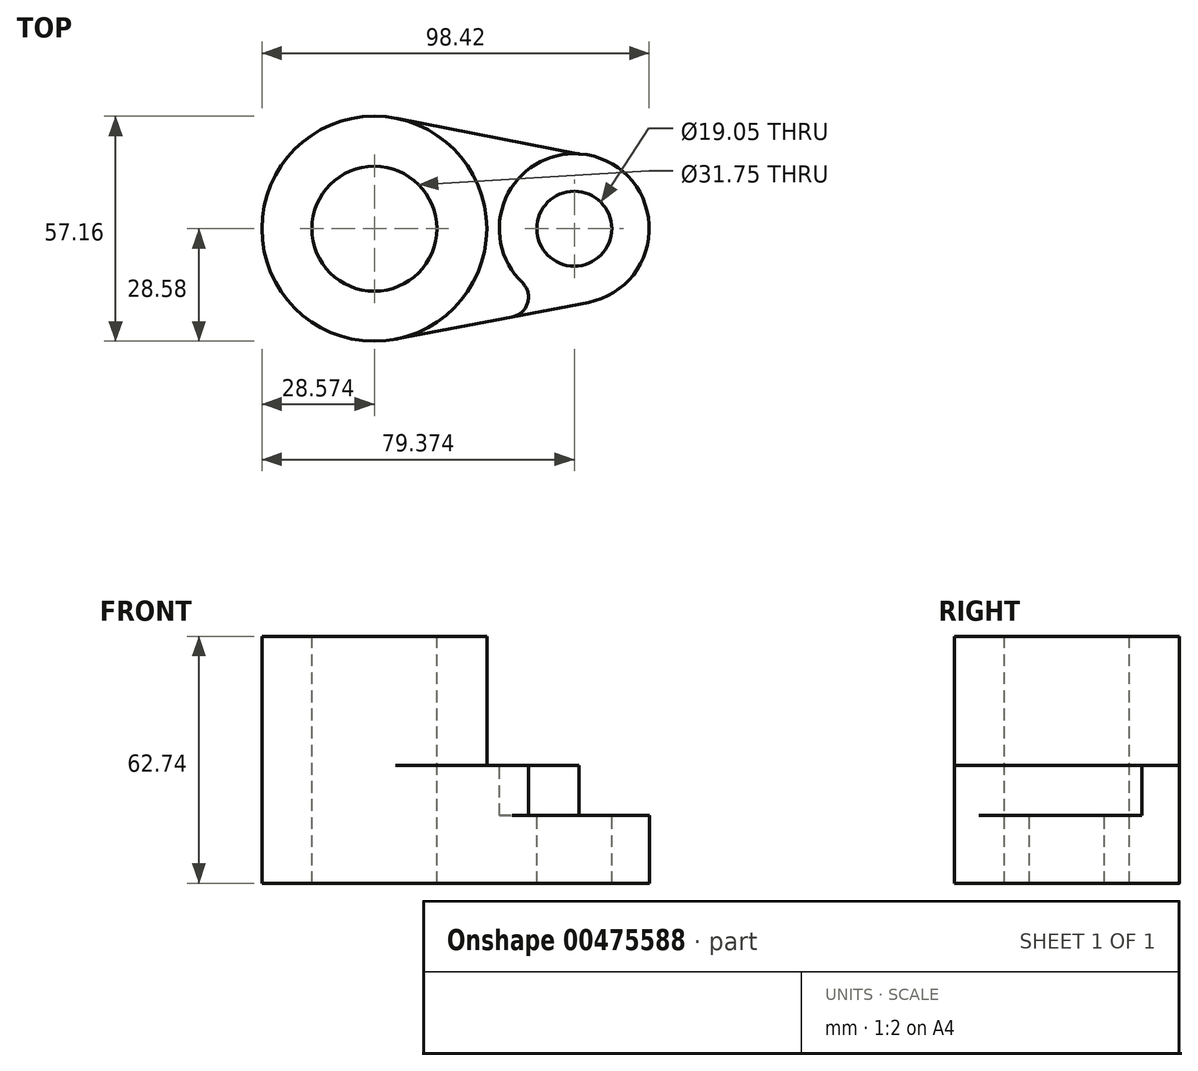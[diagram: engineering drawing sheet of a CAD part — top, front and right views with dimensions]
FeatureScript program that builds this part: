
annotation { "Feature Type Name" : "Feature", "Feature Type Description" : "" }
export const myFeature = defineFeature(function(context is Context, id is Id, definition is map)
    precondition{}
    {
        {
            var Q0;
            Q0=qCreatedBy(makeId("Top.planeOp"),FACE);
            var sketch = newSketch(context, id + "F0", { "sketchPlane" : qUnion([Q0])});
            skCircle(sketch, "E0", {"center": v(-40.5, 0) * mm, "radius": 28.58 * mm});
            skCircle(sketch, "E1", {"center": v(10.3, 0) * mm, "radius": 19.05 * mm});
            skLineSegment(sketch, "E2", {"start": v(11.55, 19) * mm, "end": v(-35.05, 28.05) * mm});
            skLineSegment(sketch, "E3", {"start": v(13.88, -18.71) * mm, "end": v(-35.14, -28.07) * mm});
            skCircle(sketch, "E4", {"center": v(-40.5, 0) * mm, "radius": 15.88 * mm});
            skCircle(sketch, "E5", {"center": v(10.3, 0) * mm, "radius": 9.53 * mm});
            skSolve(sketch);
        }
        {
            var Q0;
            {var subQ0=sQuery(id+"F0.wireOp",EDGE,"E2");Q0=makeQuery(id+"F0.imprint","IMPRINT",FACE,{"disambiguationData":[TD([[makeQuery(id+"F0.imprint","IMPRINT",EDGE,{"derivedFrom":subQ0}),1.0]])]});}
            var Q1;
            Q1=makeQuery(id+"F0.imprint","IMPRINT",FACE,{"disambiguationData":[TD([[makeQuery(id+"F0.imprint","IMPRINT",EDGE,{"derivedFrom":sQuery(id+"F0.wireOp",EDGE,"E4")}),-1.0]])]});
            var Q2;
            Q2=makeQuery(id+"F0.imprint","IMPRINT",FACE,{"disambiguationData":[TD([[makeQuery(id+"F0.imprint","IMPRINT",EDGE,{"derivedFrom":sQuery(id+"F0.wireOp",EDGE,"E5")}),-1.0]])]});
            extrude(context, id + "F1", {"entities" : qUnion([Q0, Q1, Q2]), "oppositeDirection" : true, "depth" : 29.97 * mm});
        }
        {
            var Q0;
            Q0=makeQuery(id+"F0.imprint","IMPRINT",FACE,{"disambiguationData":[TD([[makeQuery(id+"F0.imprint","IMPRINT",EDGE,{"derivedFrom":sQuery(id+"F0.wireOp",EDGE,"E4")}),-1.0]])]});
            extrude(context, id + "F2", {"entities" : qUnion([Q0]), "operationType" : NewBodyOperationType.ADD, "depth" : 32.77 * mm});
        }
        {
            var Q0;
            Q0=makeQuery(id+"F0.imprint","IMPRINT",FACE,{"disambiguationData":[TD([[makeQuery(id+"F0.imprint","IMPRINT",EDGE,{"derivedFrom":sQuery(id+"F0.wireOp",EDGE,"E5")}),-1.0]])]});
            extrude(context, id + "F3", {"entities" : qUnion([Q0]), "operationType" : NewBodyOperationType.REMOVE, "oppositeDirection" : true, "depth" : 12.7 * mm});
        }
        {
            var Q0;
            {var subQ0=sQuery(id+"F0.wireOp",EDGE,"E3");var subQ1=sQuery(id+"F0.wireOp",EDGE,"E1");Q0=makeQuery(id+"F3.boolean.opBoolean","SPLIT",EDGE,{"disambiguationData":[topologyDisambiguationEdgeConnected([makeQuery(id+"F3.opExtrude","SWEPT_FACE",FACE,{"disambiguationData":[OSD([subQ1])]})])],"derivedFrom":makeQuery(id+"F1.opExtrude","SWEPT_EDGE",EDGE,{"disambiguationData":[OSD([subQ1,subQ0])]})});}
            var Q1;
            {var subQ0=sQuery(id+"F0.wireOp",EDGE,"E2");var subQ1=sQuery(id+"F0.wireOp",EDGE,"E1");Q1=makeQuery(id+"F3.boolean.opBoolean","SPLIT",EDGE,{"disambiguationData":[topologyDisambiguationEdgeConnected([makeQuery(id+"F3.opExtrude","SWEPT_FACE",FACE,{"disambiguationData":[OSD([subQ1])]})])],"derivedFrom":makeQuery(id+"F1.opExtrude","SWEPT_EDGE",EDGE,{"disambiguationData":[OSD([subQ1,subQ0])]})});}
            fillet(context, id + "F4", {"entities" : qUnion([Q0, Q1]), "radius" : 5.08 * mm, "tangentPropagation" : true, "allowEdgeOverflow" : false});
        }
    });
